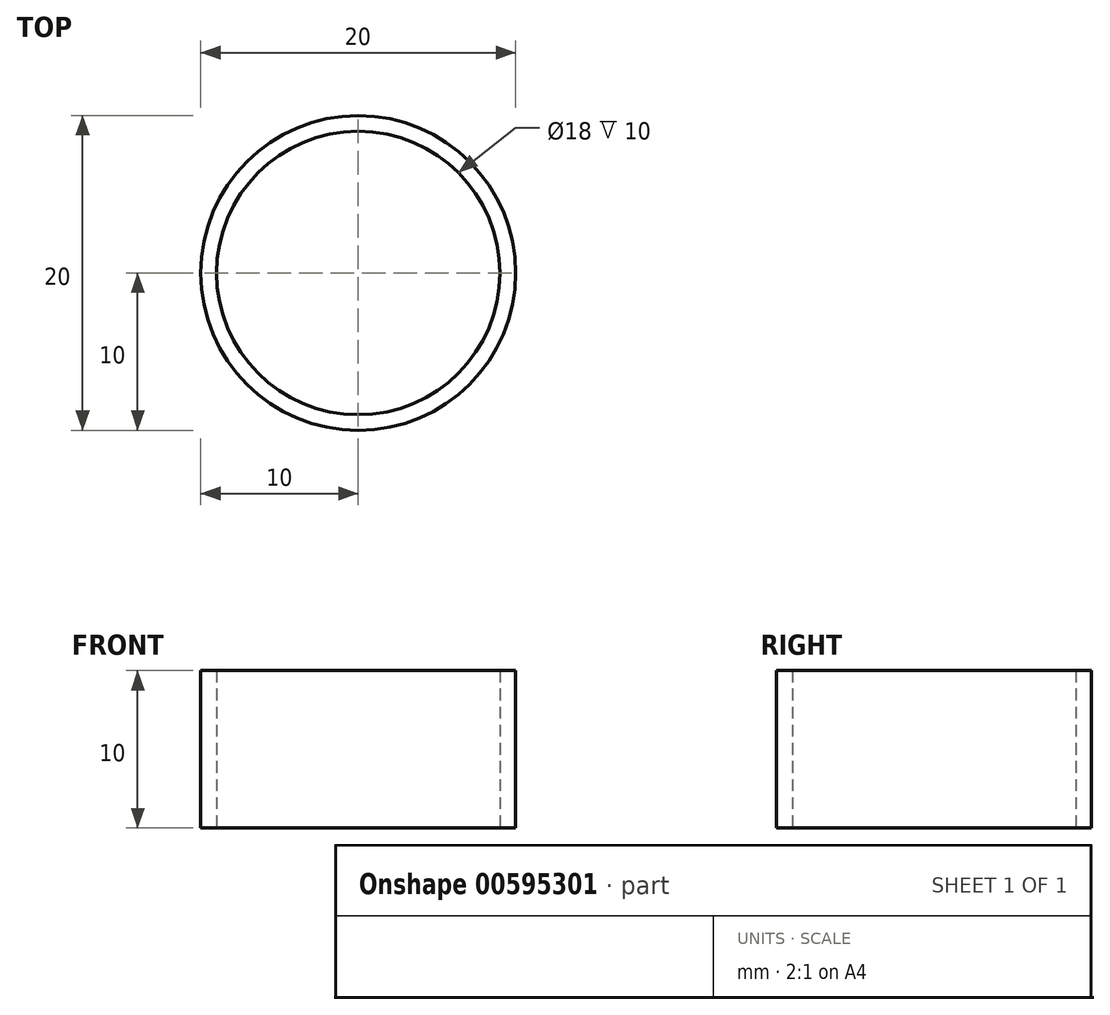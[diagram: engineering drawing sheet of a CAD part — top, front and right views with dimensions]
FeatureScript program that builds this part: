
annotation { "Feature Type Name" : "Feature", "Feature Type Description" : "" }
export const myFeature = defineFeature(function(context is Context, id is Id, definition is map)
    precondition{}
    {
        {
            var Q0;
            Q0=qCreatedBy(makeId("Top.planeOp"),FACE);
            var sketch = newSketch(context, id + "F0", { "sketchPlane" : qUnion([Q0])});
            skCircle(sketch, "E0", {"center": v(0, 0) * mm, "radius": 9 * mm});
            skCircle(sketch, "E1", {"center": v(0, 0) * mm, "radius": 10 * mm});
            skSolve(sketch);
        }
        {
            var Q0;
            Q0=makeQuery(id+"F0.imprint","IMPRINT",FACE,{"disambiguationData":[TD([[makeQuery(id+"F0.imprint","IMPRINT",EDGE,{"derivedFrom":sQuery(id+"F0.wireOp",EDGE,"E0")}),-1.0]])]});
            extrude(context, id + "F1", {"entities" : qUnion([Q0]), "depth" : 10 * mm, "offsetDistance" : 25 * mm});
        }
    });
